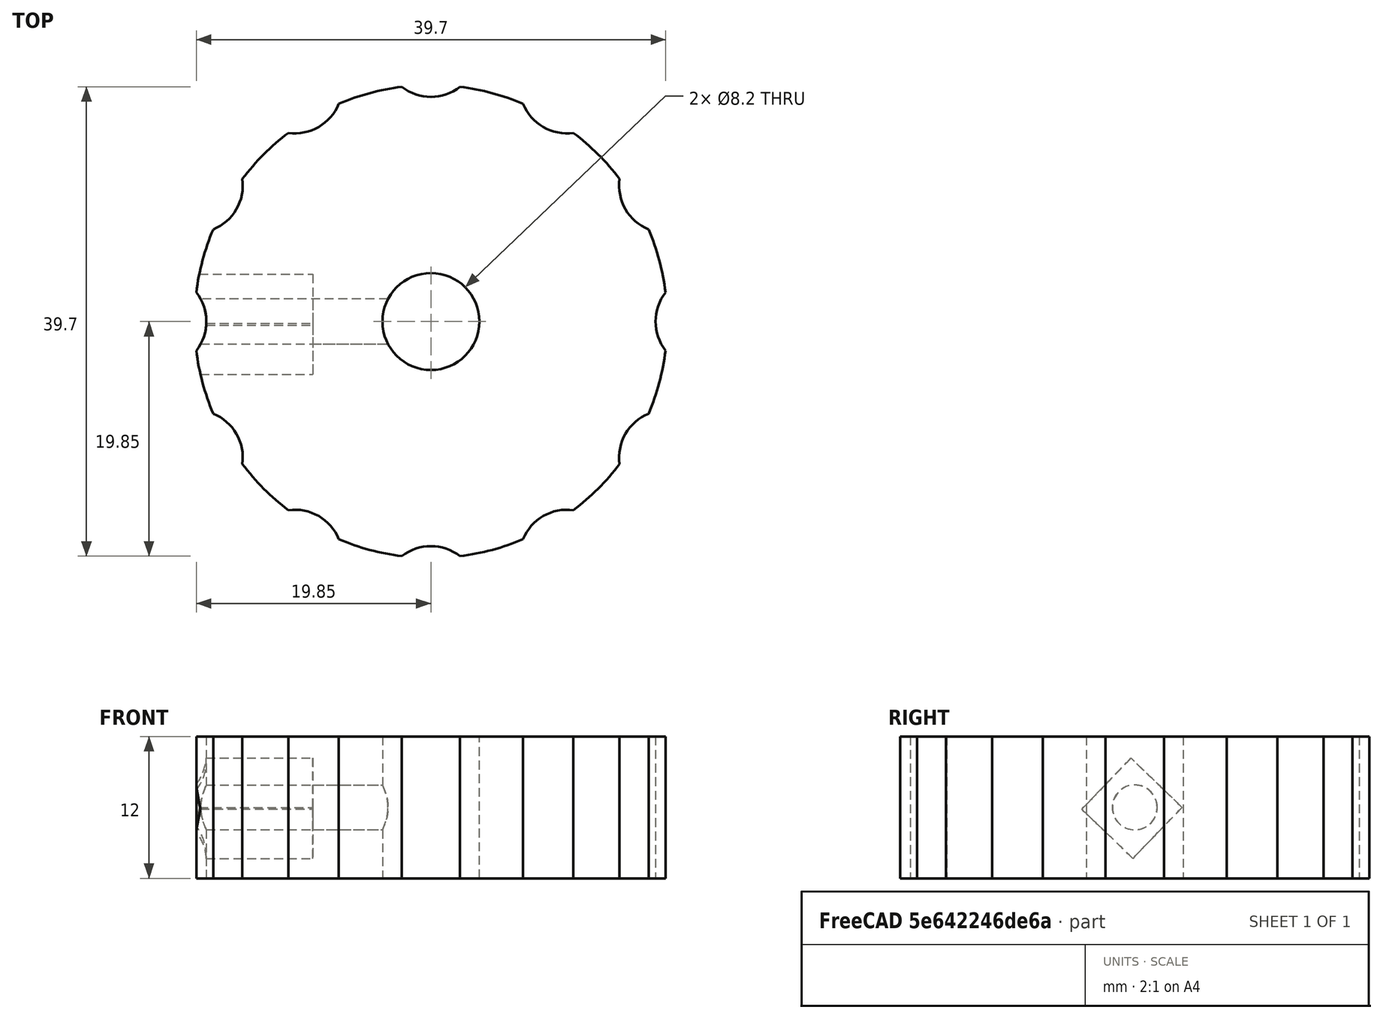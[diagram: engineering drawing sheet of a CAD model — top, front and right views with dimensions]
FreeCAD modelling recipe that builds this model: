
FCSTD DOCUMENT  (FreeCAD 0.19R)
Label: LeadScrewknob
License: All rights reserved
LicenseURL: http://en.wikipedia.org/wiki/All_rights_reserved
objects: Sketcher::SketchObject×4, PartDesign::Pocket×3, PartDesign::Pad×1, PartDesign::PolarPattern×1, PartDesign::Body×1, Part::Box×1, Part::Cut×1, Mesh::Feature×1
note: 16 computed .brp shape members not serialized (recipe doc carries the construction recipe); baked Part::Feature solids carry a one-line shape summary decoded from their .brp

FEATURE [Sketcher::SketchObject] Sketch
  FullyConstrained = true
  MapMode = 5
  Support = -> [XY_Plane]
  sketch-geometry (1):
    g0: Circle CenterX=0 CenterY=0 CenterZ=0 NormalX=0 NormalY=0 NormalZ=1 AngleXU=0 Radius=20
  constraints (2):
    c: Coincident(g0,g-1)
    c: Diameter(g0) = 40
FEATURE [PartDesign::Pad] Pad
  Direction = (1,1,1)
  Length = 12
  Length2 = 100
  Profile = -> Sketch
  Type = 0
FEATURE [Sketcher::SketchObject] Sketch001
  FullyConstrained = true
  MapMode = 5
  Placement = pos=(0,0,0) rot=(1,0,0;3.14159rad)
  Support = -> [Pad]
  sketch-geometry (1):
    g0: Circle CenterX=0 CenterY=23 CenterZ=0 NormalX=0 NormalY=0 NormalZ=1 AngleXU=0 Radius=4
  constraints (3):
    c: PointOnObject(g0,g-2)
    c: DistanceY(g0) = 23
    c: Diameter(g0) = 8
FEATURE [PartDesign::Pocket] Pocket
  BaseFeature = -> Pad
  Length = 5
  Length2 = 100
  Profile = -> Sketch001
  Type = 1
FEATURE [PartDesign::PolarPattern] PolarPattern
  Angle = 360
  Axis = -> Sketch001 [N_Axis]
  BaseFeature = -> Pocket
  Occurrences = 12
  Originals = -> [Pocket]
FEATURE [Sketcher::SketchObject] Sketch002
  FullyConstrained = true
  MapMode = 5
  Placement = pos=(0,0,0) rot=(1,0,0;3.14159rad)
  Support = -> [PolarPattern]
  sketch-geometry (1):
    g0: Circle CenterX=0 CenterY=0 CenterZ=0 NormalX=0 NormalY=0 NormalZ=1 AngleXU=0 Radius=4.1
  constraints (2):
    c: Diameter(g0) = 8.2
    c: Coincident(g0,g-1)
FEATURE [PartDesign::Pocket] Pocket001
  BaseFeature = -> PolarPattern
  Length = 5
  Length2 = 100
  Profile = -> Sketch002
  Type = 1
FEATURE [Sketcher::SketchObject] Sketch003
  FullyConstrained = true
  MapMode = 5
  Placement = pos=(0,0,0) rot=(0.57735,0.57735,0.57735;2.0944rad)
  Support = -> [YZ_Plane]
  sketch-geometry (1):
    g0: Circle CenterX=0 CenterY=6 CenterZ=0 NormalX=0 NormalY=0 NormalZ=1 AngleXU=0 Radius=1.9
  constraints (3):
    c: Diameter(g0) = 3.8
    c: DistanceY(g0) = 6
    c: PointOnObject(g0,g-2)
FEATURE [PartDesign::Pocket] Pocket002
  BaseFeature = -> Pocket001
  Length = 26
  Length2 = 100
  Profile = -> Sketch003
  Type = 0
FEATURE [PartDesign::Body] Body
  Group = -> [Sketch,Pad,Sketch001,Pocket,PolarPattern,Sketch002,Pocket001,Sketch003,Pocket002]
  Origin = -> Origin
  Tip = -> Pocket002
FEATURE [Part::Box] Box  label="Cube"
  AttacherType = Attacher::AttachEngine3D
  Height = 6
  Length = 20
  Placement = pos=(-30,4,6) rot=(1,0,0;2.37365rad)
  Width = 6
FEATURE [Part::Cut] Cut
  Base = -> Pocket002
  Tool = -> Box
FEATURE [Mesh::Feature] Mesh  label="Cut (Meshed)"
